# Revit family: 0045203+0045235 Feilo Sylvania Lighting Fixture SYLBATTEN LED8 NW TP4 E3 with SYMMETRIC REFLECTOR ACCESSORY 1500MM
name_source: partatom
category: Lighting Fixtures
revit_build: Autodesk Revit 2017 (Build: 20190507_1515(x64)
units: mm (PartAtom-declared; Revit-internal decimal feet)

## family parameters
Cut with Voids When Loaded = No
Host = Face
Light Source = Yes
OmniClass Number = 23.80.70.00
OmniClass Title = Lighting
Part Type = Normal
Room Calculation Point = No
Round Connector Dimension = Use Diameter
Shared = No

## types (2) — shared parameters
Apparent Load = 82 VA
Assembly Code = D5020200
AssetType = Fixed
AsymReflector_FEILO = No
BackReflector_FEILO = Yes
CapOffset_FEILO = 2 mm  [stored 0.00656168 ft]
ClassificationName = Uniclass2015
ClassificationValue = EF_70_80
Color Filter = 16777215
Default Elevation = 1219 mm
Description = LED batten, T8 replacement, ease of installation through 2 part push-in design of the housing (safety cable included), through wiring capability (TP4 = 4 core), sheet steel, 8348M, 79W, 106lm/W, 4000K, drive current: 450mA, CRI 80, 138° wide beam angle, electronic driver (non dimmable), integral 3 hour maintained emergency, IP20, IK07, 50,000 hrs (L70), (LxWxH) 1505x66x76mm, 5 step MacAdam ellipse, 3.7kg, white RAL9016, Class 1, 220-240V, energy class: A++, A+, A.
Dimming Lamp Color Temperature Shift = <None>
DocumentationLiterature = http://www.sylvania-lighting.com
DurationUnit = hours
ElectricShockClassification = Class I
Emit Shape Visible in Rendering = No
Emit from Rectangle Length = 26 mm
Emit from Rectangle Width = 1489 mm
ExpectedLife = 50000
FrontReflector_FEILO = Yes
Height_FEILO = 76 mm  [stored 0.249344 ft]
IfcExportAs = IfcLightFixtureType
IfcExportType = IfcLightFixtureType
ImpactProtectionIndex = IK07
IngressProtection = IP20
InputVoltage = 220-240V~
Keynote = 16500
Lamp = LED
LampColourRenderingIndex = 80
LampColourTemperature = 4000 K
LampsType = LED
Length_FEILO = 1505 mm  [stored 4.93766 ft]
LightOutputRatio = 100
LuminousEfficacy = 101.8 lm/W
Manufacturer = Feilo Sylvania
ManufacturerName = Feilo Sylvania
Material = sheet steel housing, polycarbonate diffuser
Material_1_FEILO = Body-Sylvania-Sylbatten-White
Material_2_FEILO = Body-Sylvania-Sylbatten-White
Material_3_FEILO = Diffuser-Sylvania-Sylbatten-Glow
Material_4_FEILO = Reflector-Sylvania-Sylbatten-White
Model = SYLBATTEN LED8 NW TP4 E3
ModelNumber = 0045203
ModelReference = SYLBATTEN LED8 NW TP4 E3
Name = SYLBATTEN LED8 NW TP4 E3
NominalDepth = 122 mm
NominalHeight = 91 mm
NominalLength = 1505 mm  [stored 4.93766 ft]
Photometric Web File = 0045203+0045235.ies
SymReflector_FEILO = Yes
Tilt Angle = -90.00°
Type Image = <None>
TypeName = SYLBATTEN LED8 NW TP4 E3
URL = http://www.sylvania-lighting.com
Voltage = 230 V
Weight = 3.7 kg
Width_FEILO = 66 mm  [stored 0.216535 ft]
zero-valued in all types: Cost, PowerFactor

## per-type parameters (varying)
| type | LampNominalLuminous | PowerConsumption |
| 0045203 Emergency mode | 450 lm | 81.9 W |
| 0045203 SYLBATTEN LED8 NW TP4 E3 | 8348 lm | 82 W |

note: [stored X ft] marks values corroborated as IEEE doubles in the binary element streams (Revit-internal decimal feet)

## geometry (parser evidence)
native form markers: Sweep x2
no freeform markers — native parametric forms only
